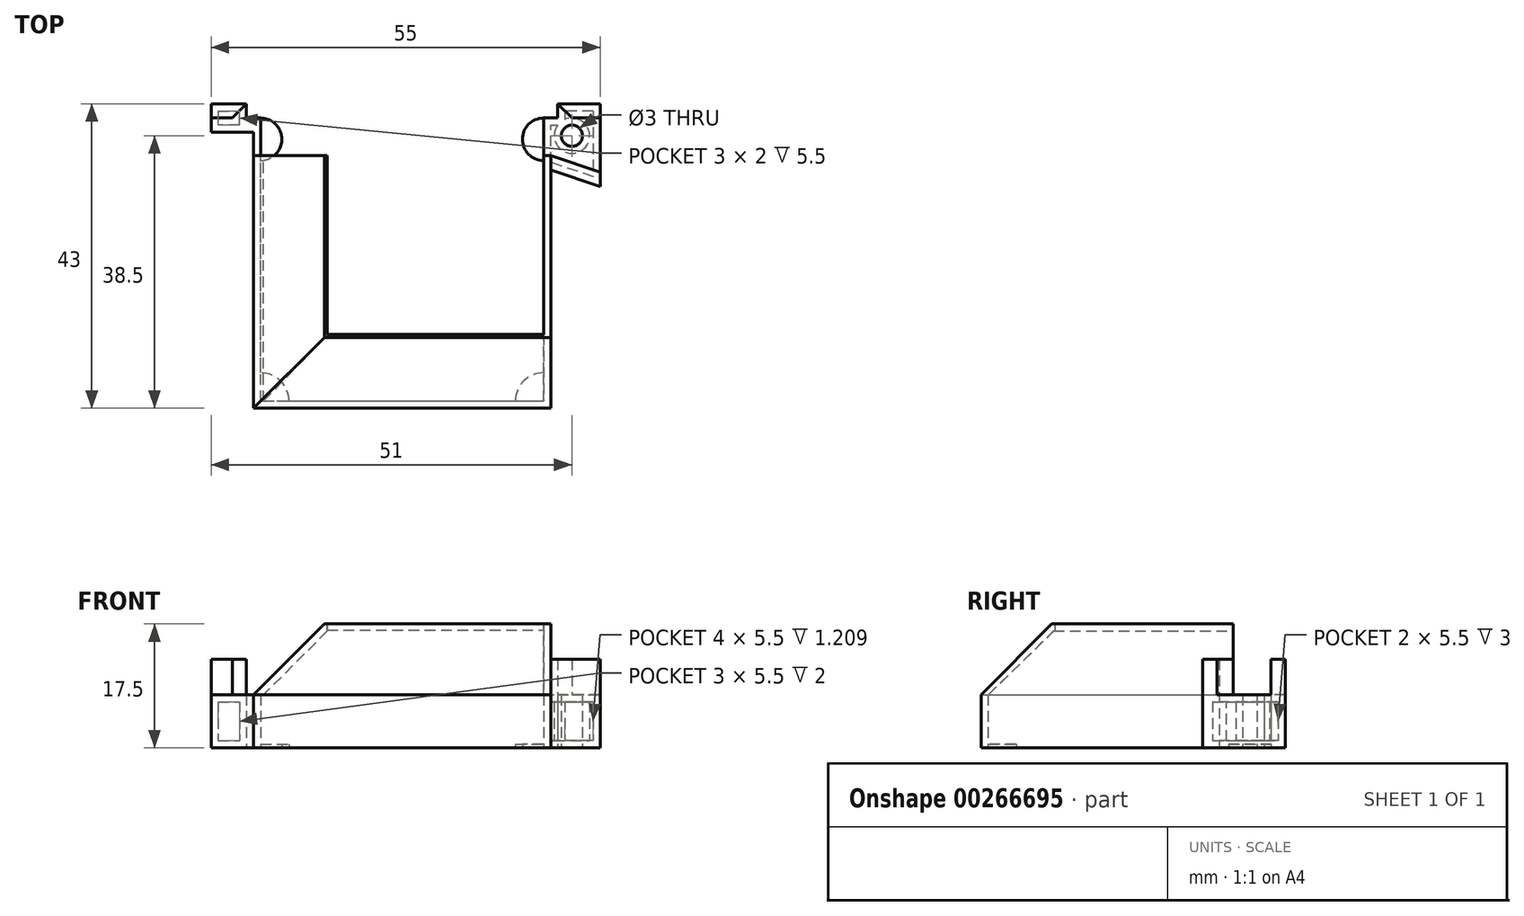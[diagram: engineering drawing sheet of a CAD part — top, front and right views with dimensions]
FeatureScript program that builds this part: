
annotation { "Feature Type Name" : "Feature", "Feature Type Description" : "" }
export const myFeature = defineFeature(function(context is Context, id is Id, definition is map)
    precondition{}
    {
        {
            var Q0;
            Q0=qCreatedBy(makeId("Top.planeOp"),FACE);
            var sketch = newSketch(context, id + "F0", { "sketchPlane" : qUnion([Q0])});
            skLineSegment(sketch, "E0", {"start": v(-20, 0) * mm, "end": v(20, 0) * mm});
            skLineSegment(sketch, "E1", {"start": v(20, 0) * mm, "end": v(20, 40) * mm});
            skLineSegment(sketch, "E2", {"start": v(-20, 0) * mm, "end": v(-20, 40) * mm});
            skLineSegment(sketch, "E3", {"start": v(20, 40) * mm, "end": v(21, 40) * mm});
            skLineSegment(sketch, "E4", {"start": v(21, 40) * mm, "end": v(21, -1) * mm});
            skLineSegment(sketch, "E5", {"start": v(21, -1) * mm, "end": v(-21, -1) * mm});
            skLineSegment(sketch, "E6", {"start": v(-21, -1) * mm, "end": v(-21, 40) * mm});
            skLineSegment(sketch, "E7", {"start": v(-21, 40) * mm, "end": v(-20, 40) * mm});
            skSolve(sketch);
        }
        {
            var Q0;
            Q0 = qSketchRegion(id + "F0", true);
            extrude(context, id + "F1", {"entities" : qUnion([Q0]), "depth" : 7.5 * mm});
        }
        {
            var Q0;
            Q0=makeQuery(id+"F1.opExtrude","CAP_FACE",FACE,{"disambiguationData":[OSD([sQuery(id+"F0.wireOp",EDGE,"E0"),sQuery(id+"F0.wireOp",EDGE,"E1"),sQuery(id+"F0.wireOp",EDGE,"E2"),sQuery(id+"F0.wireOp",EDGE,"E3"),sQuery(id+"F0.wireOp",EDGE,"E4"),sQuery(id+"F0.wireOp",EDGE,"E5"),sQuery(id+"F0.wireOp",EDGE,"E6"),sQuery(id+"F0.wireOp",EDGE,"E7")])],"isStart":true});
            var sketch = newSketch(context, id + "F2", { "sketchPlane" : qUnion([Q0])});
            skArc(sketch, "E8", {"start": v(-20, -4) * mm, "mid": v(-17.17, -2.83) * mm, "end": v(-16, 0) * mm});
            skArc(sketch, "E9", {"start": v(16, 0) * mm, "mid": v(17.17, -2.83) * mm, "end": v(20, -4) * mm});
            skLineSegment(sketch, "E10", {"start": v(-20, -4) * mm, "end": v(-20, 0) * mm});
            skLineSegment(sketch, "E11", {"start": v(16, 0) * mm, "end": v(20, 0) * mm});
            skLineSegment(sketch, "E12", {"start": v(20, 0) * mm, "end": v(20, -4) * mm});
            skLineSegment(sketch, "E13", {"start": v(-20, 0) * mm, "end": v(-16, 0) * mm});
            skArc(sketch, "E14", {"start": v(-20, -40) * mm, "mid": v(-17, -37) * mm, "end": v(-20, -34) * mm});
            skArc(sketch, "E15", {"start": v(20, -40) * mm, "mid": v(17, -37) * mm, "end": v(20, -34) * mm});
            skLineSegment(sketch, "E16", {"start": v(-20, -34) * mm, "end": v(-20, -40) * mm});
            skLineSegment(sketch, "E17", {"start": v(20, -34) * mm, "end": v(20, -40) * mm});
            skSolve(sketch);
        }
        {
            var Q0;
            Q0 = qSketchRegion(id + "F2", true);
            extrude(context, id + "F3", {"entities" : qUnion([Q0]), "operationType" : NewBodyOperationType.ADD, "oppositeDirection" : true, "depth" : .5 * mm});
        }
        {
            var Q0;
            Q0=makeQuery(id+"F3.boolean.opBoolean","MERGE",FACE,{"derivedFrom":[makeQuery(id+"F1.opExtrude","CAP_FACE",FACE,{"disambiguationData":[OSD([sQuery(id+"F0.wireOp",EDGE,"E0"),sQuery(id+"F0.wireOp",EDGE,"E1"),sQuery(id+"F0.wireOp",EDGE,"E2"),sQuery(id+"F0.wireOp",EDGE,"E3"),sQuery(id+"F0.wireOp",EDGE,"E4"),sQuery(id+"F0.wireOp",EDGE,"E5"),sQuery(id+"F0.wireOp",EDGE,"E6"),sQuery(id+"F0.wireOp",EDGE,"E7")])],"isStart":true}),makeQuery(id+"F3.opExtrude","CAP_FACE",FACE,{"disambiguationData":[OSD([sQuery(id+"F2.wireOp",EDGE,"E8"),sQuery(id+"F2.wireOp",EDGE,"E10"),sQuery(id+"F2.wireOp",EDGE,"E13")])],"isStart":true}),makeQuery(id+"F3.opExtrude","CAP_FACE",FACE,{"disambiguationData":[OSD([sQuery(id+"F2.wireOp",EDGE,"E9"),sQuery(id+"F2.wireOp",EDGE,"E11"),sQuery(id+"F2.wireOp",EDGE,"E12")])],"isStart":true}),makeQuery(id+"F3.opExtrude","CAP_FACE",FACE,{"disambiguationData":[OSD([sQuery(id+"F2.wireOp",EDGE,"E14"),sQuery(id+"F2.wireOp",EDGE,"E16")])],"isStart":true}),makeQuery(id+"F3.opExtrude","CAP_FACE",FACE,{"disambiguationData":[OSD([sQuery(id+"F2.wireOp",EDGE,"E15"),sQuery(id+"F2.wireOp",EDGE,"E17")])],"isStart":true})]});
            var sketch = newSketch(context, id + "F4", { "sketchPlane" : qUnion([Q0])});
            skLineSegment(sketch, "E18", {"start": v(20, -40) * mm, "end": v(28, -40) * mm});
            skLineSegment(sketch, "E19", {"start": v(28, -40) * mm, "end": v(28, -32.33) * mm});
            skLineSegment(sketch, "E20", {"start": v(28, -32.33) * mm, "end": v(20, -35) * mm});
            skLineSegment(sketch, "E21", {"start": v(20, -35) * mm, "end": v(20, -40) * mm});
            skLineSegment(sketch, "E22", {"start": v(20, -35) * mm, "end": v(7.72, -35) * mm, "construction": true});
            skLineSegment(sketch, "E23.bottom", {"start": v(-21, -40) * mm, "end": v(-27, -40) * mm});
            skLineSegment(sketch, "E23.top", {"start": v(-21, -38) * mm, "end": v(-27, -38) * mm});
            skLineSegment(sketch, "E23.left", {"start": v(-21, -40) * mm, "end": v(-21, -38) * mm});
            skLineSegment(sketch, "E23.right", {"start": v(-27, -40) * mm, "end": v(-27, -38) * mm});
            skSolve(sketch);
        }
        {
            var Q0;
            Q0 = qSketchRegion(id + "F4", true);
            var Q1;
            Q1=makeQuery(id+"F1.opExtrude","CAP_FACE",FACE,{"disambiguationData":[OSD([sQuery(id+"F0.wireOp",EDGE,"E0"),sQuery(id+"F0.wireOp",EDGE,"E1"),sQuery(id+"F0.wireOp",EDGE,"E2"),sQuery(id+"F0.wireOp",EDGE,"E3"),sQuery(id+"F0.wireOp",EDGE,"E4"),sQuery(id+"F0.wireOp",EDGE,"E5"),sQuery(id+"F0.wireOp",EDGE,"E6"),sQuery(id+"F0.wireOp",EDGE,"E7")])],"isStart":false});
            extrude(context, id + "F5", {"entities" : qUnion([Q0]), "operationType" : NewBodyOperationType.ADD, "endBound" : BoundingType.UP_TO_SURFACE, "oppositeDirection" : true, "endBoundEntityFace" : qUnion([Q1]), "depth" : 25 * mm});
        }
        {
            var Q0;
            Q0=makeQuery(id+"F5.boolean.opBoolean","MERGE",FACE,{"derivedFrom":[makeQuery(id+"F3.boolean.opBoolean","MERGE",FACE,{"derivedFrom":[makeQuery(id+"F1.opExtrude","CAP_FACE",FACE,{"disambiguationData":[OSD([sQuery(id+"F0.wireOp",EDGE,"E0"),sQuery(id+"F0.wireOp",EDGE,"E1"),sQuery(id+"F0.wireOp",EDGE,"E2"),sQuery(id+"F0.wireOp",EDGE,"E3"),sQuery(id+"F0.wireOp",EDGE,"E4"),sQuery(id+"F0.wireOp",EDGE,"E5"),sQuery(id+"F0.wireOp",EDGE,"E6"),sQuery(id+"F0.wireOp",EDGE,"E7")])],"isStart":true}),makeQuery(id+"F3.opExtrude","CAP_FACE",FACE,{"disambiguationData":[OSD([sQuery(id+"F2.wireOp",EDGE,"E8"),sQuery(id+"F2.wireOp",EDGE,"E10"),sQuery(id+"F2.wireOp",EDGE,"E13")])],"isStart":true}),makeQuery(id+"F3.opExtrude","CAP_FACE",FACE,{"disambiguationData":[OSD([sQuery(id+"F2.wireOp",EDGE,"E9"),sQuery(id+"F2.wireOp",EDGE,"E11"),sQuery(id+"F2.wireOp",EDGE,"E12")])],"isStart":true}),makeQuery(id+"F3.opExtrude","CAP_FACE",FACE,{"disambiguationData":[OSD([sQuery(id+"F2.wireOp",EDGE,"E14"),sQuery(id+"F2.wireOp",EDGE,"E16")])],"isStart":true}),makeQuery(id+"F3.opExtrude","CAP_FACE",FACE,{"disambiguationData":[OSD([sQuery(id+"F2.wireOp",EDGE,"E15"),sQuery(id+"F2.wireOp",EDGE,"E17")])],"isStart":true})]}),makeQuery(id+"F5.opExtrude","CAP_FACE",FACE,{"disambiguationData":[OSD([sQuery(id+"F4.wireOp",EDGE,"E18"),sQuery(id+"F4.wireOp",EDGE,"E19"),sQuery(id+"F4.wireOp",EDGE,"E20"),sQuery(id+"F4.wireOp",EDGE,"E21")])],"isStart":true}),makeQuery(id+"F5.opExtrude","CAP_FACE",FACE,{"disambiguationData":[OSD([sQuery(id+"F4.wireOp",EDGE,"E23.bottom"),sQuery(id+"F4.wireOp",EDGE,"E23.top"),sQuery(id+"F4.wireOp",EDGE,"E23.left"),sQuery(id+"F4.wireOp",EDGE,"E23.right")])],"isStart":true})]});
            var sketch = newSketch(context, id + "F6", { "sketchPlane" : qUnion([Q0])});
            skLineSegment(sketch, "E24", {"start": v(20, -37.5) * mm, "end": v(24, -37.5) * mm, "construction": true});
            skCircle(sketch, "E25", {"center": v(24, -37.5) * mm, "radius": 1.5 * mm});
            skSolve(sketch);
        }
        {
            var Q0;
            Q0 = qSketchRegion(id + "F6", true);
            extrude(context, id + "F7", {"entities" : qUnion([Q0]), "operationType" : NewBodyOperationType.REMOVE, "endBound" : BoundingType.THROUGH_ALL, "oppositeDirection" : true, "depth" : 25 * mm});
        }
        {
            var Q0;
            Q0=makeQuery(id+"F5.boolean.opBoolean","MERGE",FACE,{"derivedFrom":[makeQuery(id+"F3.boolean.opBoolean","MERGE",FACE,{"derivedFrom":[makeQuery(id+"F1.opExtrude","CAP_FACE",FACE,{"disambiguationData":[OSD([sQuery(id+"F0.wireOp",EDGE,"E0"),sQuery(id+"F0.wireOp",EDGE,"E1"),sQuery(id+"F0.wireOp",EDGE,"E2"),sQuery(id+"F0.wireOp",EDGE,"E3"),sQuery(id+"F0.wireOp",EDGE,"E4"),sQuery(id+"F0.wireOp",EDGE,"E5"),sQuery(id+"F0.wireOp",EDGE,"E6"),sQuery(id+"F0.wireOp",EDGE,"E7")])],"isStart":true}),makeQuery(id+"F3.opExtrude","CAP_FACE",FACE,{"disambiguationData":[OSD([sQuery(id+"F2.wireOp",EDGE,"E8"),sQuery(id+"F2.wireOp",EDGE,"E10"),sQuery(id+"F2.wireOp",EDGE,"E13")])],"isStart":true}),makeQuery(id+"F3.opExtrude","CAP_FACE",FACE,{"disambiguationData":[OSD([sQuery(id+"F2.wireOp",EDGE,"E9"),sQuery(id+"F2.wireOp",EDGE,"E11"),sQuery(id+"F2.wireOp",EDGE,"E12")])],"isStart":true}),makeQuery(id+"F3.opExtrude","CAP_FACE",FACE,{"disambiguationData":[OSD([sQuery(id+"F2.wireOp",EDGE,"E14"),sQuery(id+"F2.wireOp",EDGE,"E16")])],"isStart":true}),makeQuery(id+"F3.opExtrude","CAP_FACE",FACE,{"disambiguationData":[OSD([sQuery(id+"F2.wireOp",EDGE,"E15"),sQuery(id+"F2.wireOp",EDGE,"E17")])],"isStart":true})]}),makeQuery(id+"F5.opExtrude","CAP_FACE",FACE,{"disambiguationData":[OSD([sQuery(id+"F4.wireOp",EDGE,"E18"),sQuery(id+"F4.wireOp",EDGE,"E19"),sQuery(id+"F4.wireOp",EDGE,"E20"),sQuery(id+"F4.wireOp",EDGE,"E21")])],"isStart":true})]});
            var sketch = newSketch(context, id + "F8", { "sketchPlane" : qUnion([Q0])});
            skLineSegment(sketch, "E26", {"start": v(28, -40) * mm, "end": v(28, -42) * mm});
            skLineSegment(sketch, "E27", {"start": v(28, -42) * mm, "end": v(22, -42) * mm});
            skLineSegment(sketch, "E28", {"start": v(22, -42) * mm, "end": v(22, -40) * mm});
            skLineSegment(sketch, "E29", {"start": v(22, -40) * mm, "end": v(28, -40) * mm});
            skLineSegment(sketch, "E30", {"start": v(28, -32.33) * mm, "end": v(28, -30.33) * mm});
            skLineSegment(sketch, "E31", {"start": v(28, -30.33) * mm, "end": v(21, -32.67) * mm});
            skLineSegment(sketch, "E32", {"start": v(21, -32.67) * mm, "end": v(21, -34.67) * mm});
            skLineSegment(sketch, "E33", {"start": v(21, -34.67) * mm, "end": v(28, -32.33) * mm});
            skLineSegment(sketch, "E34.bottom", {"start": v(-27, -40) * mm, "end": v(-22, -40) * mm});
            skLineSegment(sketch, "E34.top", {"start": v(-27, -42) * mm, "end": v(-22, -42) * mm});
            skLineSegment(sketch, "E34.left", {"start": v(-27, -40) * mm, "end": v(-27, -42) * mm});
            skLineSegment(sketch, "E34.right", {"start": v(-22, -40) * mm, "end": v(-22, -42) * mm});
            skSolve(sketch);
        }
        {
            var Q0;
            Q0 = qSketchRegion(id + "F8", true);
            extrude(context, id + "F9", {"entities" : qUnion([Q0]), "operationType" : NewBodyOperationType.ADD, "oppositeDirection" : true, "depth" : 12.5 * mm});
        }
        {
            var Q0;
            {var subQ0=sQuery(id+"F0.wireOp",EDGE,"E3");var subQ1=sQuery(id+"F4.wireOp",EDGE,"E18");var subQ2=sQuery(id+"F8.wireOp",EDGE,"E28");Q0=makeQuery(id+"F9.boolean.opBoolean","SPLIT",EDGE,{"disambiguationData":[topologyDisambiguationEdgeConnected([makeQuery(id+"F1.opExtrude","SWEPT_FACE",FACE,{"disambiguationData":[OSD([subQ0])]})])],"derivedFrom":makeQuery(id+"F9.opExtrude","SWEPT_EDGE",EDGE,{"disambiguationData":[OSD([subQ0,subQ1,subQ2,sQuery(id+"F8.wireOp",EDGE,"E29")])]})});}
            var Q1;
            {var subQ0=sQuery(id+"F0.wireOp",EDGE,"E7");var subQ1=sQuery(id+"F4.wireOp",EDGE,"E23.bottom");var subQ2=sQuery(id+"F8.wireOp",EDGE,"E34.right");Q1=makeQuery(id+"F9.boolean.opBoolean","SPLIT",EDGE,{"disambiguationData":[topologyDisambiguationEdgeConnected([makeQuery(id+"F1.opExtrude","SWEPT_FACE",FACE,{"disambiguationData":[OSD([subQ0])]})])],"derivedFrom":makeQuery(id+"F9.opExtrude","SWEPT_EDGE",EDGE,{"disambiguationData":[OSD([subQ0,subQ1,sQuery(id+"F8.wireOp",EDGE,"E34.bottom"),subQ2])]})});}
            var Q2;
            Q2=makeQuery(id+"F5.opExtrude","SWEPT_EDGE",EDGE,{"disambiguationData":[OSD([sQuery(id+"F0.wireOp",EDGE,"E6"),sQuery(id+"F4.wireOp",EDGE,"E23.top"),sQuery(id+"F4.wireOp",EDGE,"E23.left")])]});
            chamfer(context, id + "F10", {"entities" : qUnion([Q0, Q1, Q2]), "width" : 2 * mm, "tangentPropagation" : true});
        }
        {
            var Q0;
            {var subQ0=sQuery(id+"F0.wireOp",EDGE,"E7");var subQ1=sQuery(id+"F0.wireOp",EDGE,"E6");var subQ2=sQuery(id+"F0.wireOp",EDGE,"E5");var subQ3=sQuery(id+"F0.wireOp",EDGE,"E4");var subQ4=sQuery(id+"F0.wireOp",EDGE,"E3");var subQ5=sQuery(id+"F0.wireOp",EDGE,"E2");var subQ6=sQuery(id+"F0.wireOp",EDGE,"E1");var subQ7=sQuery(id+"F0.wireOp",EDGE,"E0");Q0=makeQuery(id+"F5.boolean.opBoolean","MERGE",FACE,{"derivedFrom":[makeQuery(id+"F1.opExtrude","CAP_FACE",FACE,{"disambiguationData":[OSD([subQ7,subQ6,subQ5,subQ4,subQ3,subQ2,subQ1,subQ0])],"isStart":false}),makeQuery(id+"F5.opExtrude","CAP_FACE",FACE,{"disambiguationData":[OSD([subQ7,subQ6,subQ5,subQ4,subQ3,subQ2,subQ1,subQ0]),ownerDisambiguation([makeQuery(id+"F5.opExtrude","SWEPT_BODY",BODY,{"disambiguationData":[OSD([sQuery(id+"F4.wireOp",EDGE,"E18"),sQuery(id+"F4.wireOp",EDGE,"E19"),sQuery(id+"F4.wireOp",EDGE,"E20"),sQuery(id+"F4.wireOp",EDGE,"E21")])]})])],"isStart":false}),makeQuery(id+"F5.opExtrude","CAP_FACE",FACE,{"disambiguationData":[OSD([subQ7,subQ6,subQ5,subQ4,subQ3,subQ2,subQ1,subQ0]),ownerDisambiguation([makeQuery(id+"F5.opExtrude","SWEPT_BODY",BODY,{"disambiguationData":[OSD([sQuery(id+"F4.wireOp",EDGE,"E23.bottom"),sQuery(id+"F4.wireOp",EDGE,"E23.top"),sQuery(id+"F4.wireOp",EDGE,"E23.left"),sQuery(id+"F4.wireOp",EDGE,"E23.right")])]})])],"isStart":false})]});}
            var sketch = newSketch(context, id + "F11", { "sketchPlane" : qUnion([Q0])});
            skLineSegment(sketch, "E35.bottom", {"start": v(-21, -1) * mm, "end": v(21, -1) * mm});
            skLineSegment(sketch, "E35.top", {"start": v(-21, 34.67) * mm, "end": v(21, 34.67) * mm});
            skLineSegment(sketch, "E35.left", {"start": v(-21, -1) * mm, "end": v(-21, 34.67) * mm});
            skLineSegment(sketch, "E35.right", {"start": v(21, -1) * mm, "end": v(21, 34.67) * mm});
            skSolve(sketch);
        }
        {
            var Q0;
            Q0 = qSketchRegion(id + "F11", true);
            extrude(context, id + "F12", {"entities" : qUnion([Q0]), "operationType" : NewBodyOperationType.ADD, "depth" : 10 * mm});
        }
        {
            var Q0;
            Q0=makeQuery(id+"F12.opExtrude","SWEPT_FACE",FACE,{"disambiguationData":[OSD([sQuery(id+"F11.wireOp",EDGE,"E35.top")])]});
            var sketch = newSketch(context, id + "F13", { "sketchPlane" : qUnion([Q0])});
            skLineSegment(sketch, "E36", {"start": v(21, 7.5) * mm, "end": v(11, 17.5) * mm});
            skLineSegment(sketch, "E37", {"start": v(11, 17.5) * mm, "end": v(21, 17.5) * mm});
            skLineSegment(sketch, "E38", {"start": v(21, 17.5) * mm, "end": v(21, 7.5) * mm});
            skSolve(sketch);
        }
        {
            var Q0;
            Q0 = qSketchRegion(id + "F13", true);
            var Q1;
            Q1=makeQuery(id+"F12.boolean.opBoolean","MERGE",FACE,{"derivedFrom":[makeQuery(id+"F1.opExtrude","SWEPT_FACE",FACE,{"disambiguationData":[OSD([sQuery(id+"F0.wireOp",EDGE,"E5")])]}),makeQuery(id+"F12.opExtrude","SWEPT_FACE",FACE,{"disambiguationData":[OSD([sQuery(id+"F11.wireOp",EDGE,"E35.bottom")])]})]});
            extrude(context, id + "F14", {"entities" : qUnion([Q0]), "operationType" : NewBodyOperationType.REMOVE, "endBound" : BoundingType.UP_TO_SURFACE, "oppositeDirection" : true, "endBoundEntityFace" : qUnion([Q1]), "depth" : 25 * mm});
        }
        {
            var Q0;
            Q0=makeQuery(id+"F12.boolean.opBoolean","MERGE",FACE,{"derivedFrom":[makeQuery(id+"F1.opExtrude","SWEPT_FACE",FACE,{"disambiguationData":[OSD([sQuery(id+"F0.wireOp",EDGE,"E6")])]}),makeQuery(id+"F12.opExtrude","SWEPT_FACE",FACE,{"disambiguationData":[OSD([sQuery(id+"F11.wireOp",EDGE,"E35.left")])]})]});
            var sketch = newSketch(context, id + "F15", { "sketchPlane" : qUnion([Q0])});
            skLineSegment(sketch, "E39", {"start": v(1, 7.5) * mm, "end": v(-11.2, 19.7) * mm});
            skLineSegment(sketch, "E40", {"start": v(-11.2, 19.7) * mm, "end": v(1, 19.7) * mm});
            skLineSegment(sketch, "E41", {"start": v(1, 19.7) * mm, "end": v(1, 7.5) * mm});
            skSolve(sketch);
        }
        {
            var Q0;
            Q0 = qSketchRegion(id + "F15", true);
            extrude(context, id + "F16", {"entities" : qUnion([Q0]), "operationType" : NewBodyOperationType.REMOVE, "endBound" : BoundingType.THROUGH_ALL, "oppositeDirection" : true, "depth" : 25 * mm});
        }
        {
            var Q0;
            Q0=makeQuery(id+"F12.opExtrude","CAP_FACE",FACE,{"disambiguationData":[OSD([sQuery(id+"F11.wireOp",EDGE,"E35.bottom"),sQuery(id+"F11.wireOp",EDGE,"E35.top"),sQuery(id+"F11.wireOp",EDGE,"E35.left"),sQuery(id+"F11.wireOp",EDGE,"E35.right")])],"isStart":true});
            shell(context, id + "F17", {"entities" : qUnion([Q0]), "thickness" : 1 * mm});
        }
        {
            var Q0;
            Q0=makeQuery(id+"F17.opShell","OFFSET_FACE",FACE,{"disambiguationData":[OSD([sQuery(id+"F11.wireOp",EDGE,"E35.bottom"),sQuery(id+"F11.wireOp",EDGE,"E35.top"),sQuery(id+"F11.wireOp",EDGE,"E35.left"),sQuery(id+"F11.wireOp",EDGE,"E35.right")])]});
            extrude(context, id + "F18", {"entities" : qUnion([Q0]), "operationType" : NewBodyOperationType.REMOVE, "oppositeDirection" : true, "depth" : 25 * mm});
        }
        {
            var Q0;
            {var subQ0=sQuery(id+"F11.wireOp",EDGE,"E35.top");Q0=makeQuery(id+"F18.boolean.opBoolean","MERGE",FACE,{"derivedFrom":[makeQuery(id+"F17.opShell","OFFSET_FACE",FACE,{"disambiguationData":[OSD([subQ0])]}),makeQuery(id+"F18.opExtrude","SWEPT_FACE",FACE,{"disambiguationData":[OSD([subQ0])]})]});}
            extrude(context, id + "F19", {"entities" : qUnion([Q0]), "operationType" : NewBodyOperationType.REMOVE, "oppositeDirection" : true, "depth" : 25 * mm});
        }
        {
            var Q0;
            Q0=makeQuery(id+"F17.opShell","TWEAK_EDGE",EDGE,{"derivedFrom":[makeQuery(id+"F12.opExtrude","CAP_FACE",FACE,{"disambiguationData":[OSD([sQuery(id+"F11.wireOp",EDGE,"E35.bottom"),sQuery(id+"F11.wireOp",EDGE,"E35.top"),sQuery(id+"F11.wireOp",EDGE,"E35.left"),sQuery(id+"F11.wireOp",EDGE,"E35.right")])],"isStart":true}),makeQuery(id+"F16.boolean.opBoolean","COPY",FACE,{"derivedFrom":makeQuery(id+"F16.opExtrude","SWEPT_FACE",FACE,{"disambiguationData":[OSD([sQuery(id+"F15.wireOp",EDGE,"E39")])]})})]});
            var Q1;
            {var subQ0=sQuery(id+"F13.wireOp",EDGE,"E36");var subQ1=sQuery(id+"F11.wireOp",EDGE,"E35.right");var subQ2=sQuery(id+"F11.wireOp",EDGE,"E35.left");var subQ3=sQuery(id+"F11.wireOp",EDGE,"E35.top");var subQ4=sQuery(id+"F11.wireOp",EDGE,"E35.bottom");Q1=makeQuery(id+"F19.boolean.opBoolean","MERGE",EDGE,{"derivedFrom":[makeQuery(id+"F17.opShell","TWEAK_EDGE",EDGE,{"derivedFrom":[makeQuery(id+"F12.opExtrude","CAP_FACE",FACE,{"disambiguationData":[OSD([subQ4,subQ3,subQ2,subQ1])],"isStart":true}),makeQuery(id+"F14.boolean.opBoolean","COPY",FACE,{"derivedFrom":makeQuery(id+"F14.opExtrude","SWEPT_FACE",FACE,{"disambiguationData":[OSD([subQ0])]})})]}),makeQuery(id+"F19.opExtrude","SWEPT_EDGE",EDGE,{"disambiguationData":[OSD([subQ4,subQ3,subQ2,subQ1,subQ0])]})]});}
            chamfer(context, id + "F20", {"entities" : qUnion([Q0, Q1]), "chamferType" : ChamferType.TWO_OFFSETS, "width1" : .4 * mm, "oppositeDirection" : false, "width2" : 20 * mm, "tangentPropagation" : true});
        }
    });
